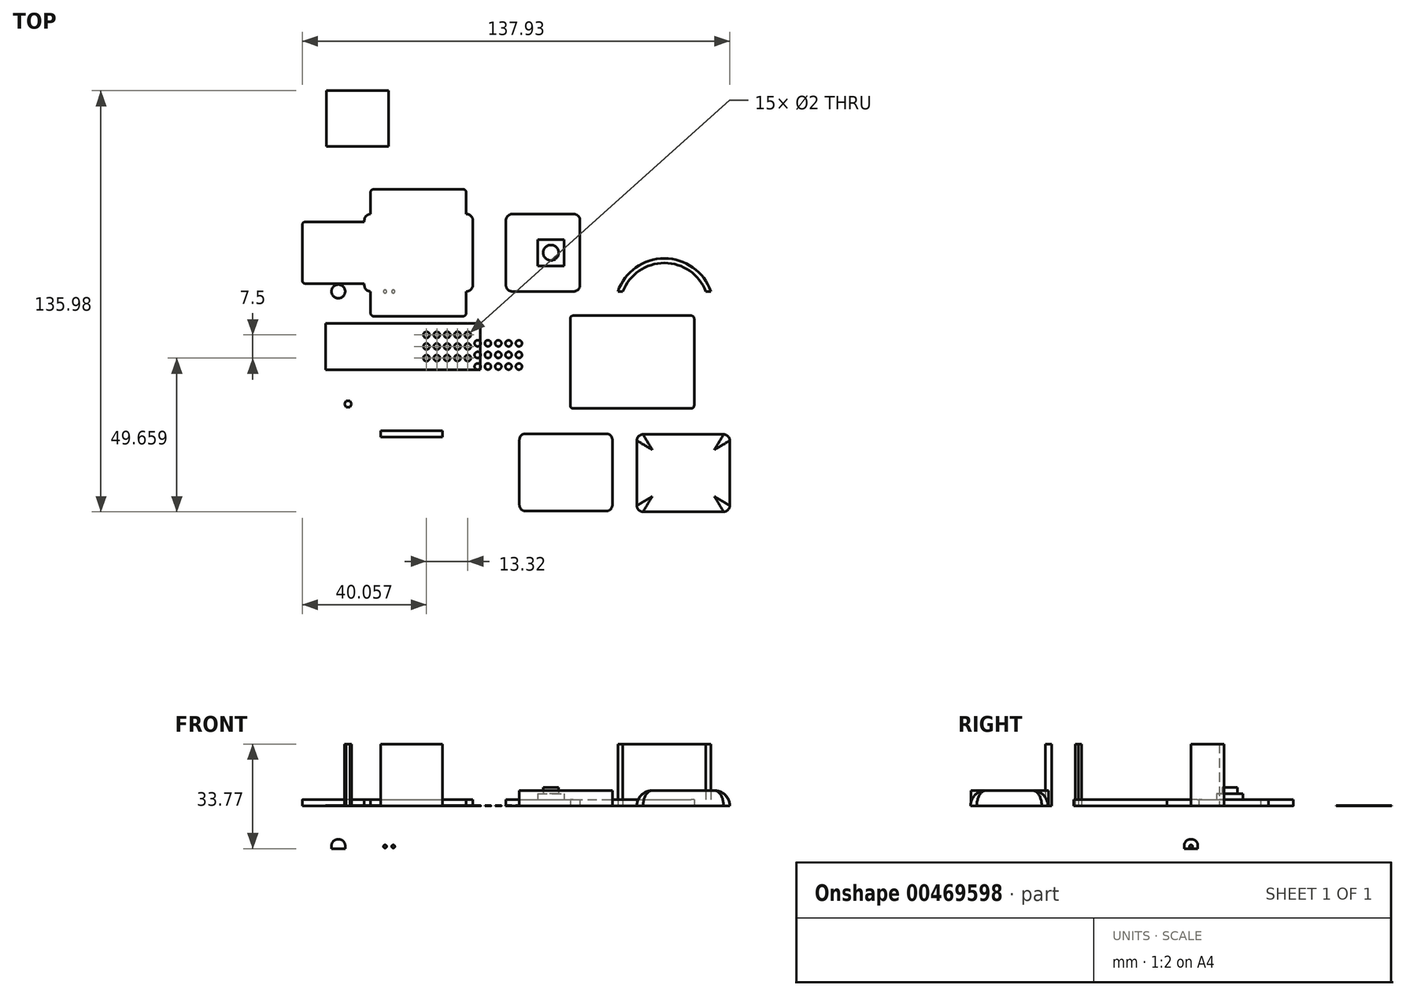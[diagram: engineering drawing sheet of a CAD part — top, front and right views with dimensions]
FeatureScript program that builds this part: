
annotation { "Feature Type Name" : "Feature", "Feature Type Description" : "" }
export const myFeature = defineFeature(function(context is Context, id is Id, definition is map)
    precondition{}
    {
        {
            var Q0;
            Q0=qCreatedBy(makeId("Top.planeOp"),FACE);
            var sketch = newSketch(context, id + "F0", { "sketchPlane" : qUnion([Q0])});
            skLineSegment(sketch, "E0.bottom", {"start": v(2, 0) * mm, "end": v(21.86, 0) * mm});
            skLineSegment(sketch, "E0.top", {"start": v(2, 25) * mm, "end": v(21.86, 25) * mm});
            skLineSegment(sketch, "E0.left", {"start": v(0, 2) * mm, "end": v(0, 23) * mm});
            skLineSegment(sketch, "E0.right", {"start": v(23.86, 2) * mm, "end": v(23.86, 23) * mm});
            skPoint(sketch, "E1.visualSharp", {"position": v(0, 25) * mm});
            skArc(sketch, "E1.filletArc", {"start": v(2, 25) * mm, "mid": v(0.59, 24.41) * mm, "end": v(0, 23) * mm});
            skPoint(sketch, "E2.visualSharp", {"position": v(0, 0) * mm});
            skArc(sketch, "E2.filletArc", {"start": v(0, 2) * mm, "mid": v(0.59, 0.59) * mm, "end": v(2, 0) * mm});
            skPoint(sketch, "E3.visualSharp", {"position": v(23.86, 25) * mm});
            skArc(sketch, "E3.filletArc", {"start": v(23.86, 23) * mm, "mid": v(23.28, 24.41) * mm, "end": v(21.86, 25) * mm});
            skPoint(sketch, "E4.visualSharp", {"position": v(23.86, 0) * mm});
            skArc(sketch, "E4.filletArc", {"start": v(21.86, 0) * mm, "mid": v(23.28, 0.59) * mm, "end": v(23.86, 2) * mm});
            skPoint(sketch, "E5.startSnap0", {"position": v(0.59, 0.59) * mm});
            skLineSegment(sketch, "E6", {"start": v(0, 25) * mm, "end": v(14.5, 25) * mm});
            skLineSegment(sketch, "E7", {"start": v(0, 0) * mm, "end": v(14.5, 0) * mm});
            skLineSegment(sketch, "E8", {"start": v(10.25, 12.5) * mm, "end": v(10.25, 16.75) * mm});
            skLineSegment(sketch, "E9.bottom", {"start": v(10.25, 16.75) * mm, "end": v(18.75, 16.75) * mm});
            skLineSegment(sketch, "E9.top", {"start": v(10.25, 8.25) * mm, "end": v(18.75, 8.25) * mm});
            skLineSegment(sketch, "E9.left", {"start": v(10.25, 16.75) * mm, "end": v(10.25, 8.25) * mm});
            skLineSegment(sketch, "E9.right", {"start": v(18.75, 16.75) * mm, "end": v(18.75, 8.25) * mm});
            skCircle(sketch, "E10", {"center": v(14.5, 12.5) * mm, "radius": 2.5 * mm});
            skPoint(sketch, "E10.centerSnap0", {"position": v(14.5, 16.75) * mm});
            skSolve(sketch);
        }
        {
            var Q0;
            Q0 = qSketchRegion(id + "F0", true);
            extrude(context, id + "F1", {"entities" : qUnion([Q0]), "depth" : 2 * mm});
        }
        {
            var Q0;
            {var subQ3=sQuery(id+"F0.wireOp",EDGE,"E9.bottom");Q0=makeQuery(id+"F0.imprint","IMPRINT",FACE,{"disambiguationData":[TD([[makeQuery(id+"F0.imprint","IMPRINT",EDGE,{"derivedFrom":subQ3}),-1.0]])]});}
            extrude(context, id + "F2", {"entities" : qUnion([Q0]), "operationType" : NewBodyOperationType.ADD, "depth" : 4 * mm});
        }
        {
            var Q0;
            Q0=makeQuery(id+"F0.imprint","IMPRINT",FACE,{"disambiguationData":[TD([[makeQuery(id+"F0.imprint","IMPRINT",EDGE,{"derivedFrom":sQuery(id+"F0.wireOp",EDGE,"E10")}),1.0]])]});
            extrude(context, id + "F3", {"entities" : qUnion([Q0]), "operationType" : NewBodyOperationType.ADD, "depth" : 6 * mm});
        }
        {
            var Q0;
            Q0=qCreatedBy(makeId("Top.planeOp"),FACE);
            var sketch = newSketch(context, id + "F4", { "sketchPlane" : qUnion([Q0])});
            skLineSegment(sketch, "E11.bottom", {"start": v(-43.71, 0) * mm, "end": v(-12.71, 0) * mm});
            skLineSegment(sketch, "E11.top", {"start": v(-43.71, 25) * mm, "end": v(-12.71, 25) * mm});
            skLineSegment(sketch, "E11.left", {"start": v(-45.71, 0) * mm, "end": v(-45.71, 23) * mm});
            skLineSegment(sketch, "E11.right", {"start": v(-10.71, 2) * mm, "end": v(-10.71, 23) * mm});
            skLineSegment(sketch, "E12", {"start": v(-45.71, 2) * mm, "end": v(-45.71, 2.5) * mm});
            skLineSegment(sketch, "E13.bottom", {"start": v(-45.71, 2.5) * mm, "end": v(-64.71, 2.5) * mm});
            skLineSegment(sketch, "E13.top", {"start": v(-45.71, 22.5) * mm, "end": v(-64.71, 22.5) * mm});
            skLineSegment(sketch, "E13.left", {"start": v(-45.71, 2.5) * mm, "end": v(-45.71, 22.5) * mm});
            skLineSegment(sketch, "E13.right", {"start": v(-65.71, 3.5) * mm, "end": v(-65.71, 21.5) * mm});
            skPoint(sketch, "E14.visualSharp", {"position": v(-45.71, 25) * mm});
            skArc(sketch, "E14.filletArc", {"start": v(-43.71, 25) * mm, "mid": v(-45.13, 24.41) * mm, "end": v(-45.71, 23) * mm});
            skPoint(sketch, "E15.visualSharp", {"position": v(-45.71, 0) * mm});
            skArc(sketch, "E15.filletArc", {"start": v(-45.71, 2) * mm, "mid": v(-45.13, 0.59) * mm, "end": v(-43.71, 0) * mm});
            skPoint(sketch, "E16.visualSharp", {"position": v(-10.71, 25) * mm});
            skArc(sketch, "E16.filletArc", {"start": v(-10.71, 23) * mm, "mid": v(-11.3, 24.41) * mm, "end": v(-12.71, 25) * mm});
            skPoint(sketch, "E17.visualSharp", {"position": v(-10.71, 0) * mm});
            skArc(sketch, "E17.filletArc", {"start": v(-12.71, 0) * mm, "mid": v(-11.3, 0.59) * mm, "end": v(-10.71, 2) * mm});
            skLineSegment(sketch, "E18.bottom", {"start": v(-43.71, 25) * mm, "end": v(-12.85, 25) * mm});
            skLineSegment(sketch, "E18.top", {"start": v(-42.71, 33) * mm, "end": v(-13.85, 33) * mm});
            skLineSegment(sketch, "E18.left", {"start": v(-43.71, 25) * mm, "end": v(-43.71, 32) * mm});
            skLineSegment(sketch, "E18.right", {"start": v(-12.85, 25) * mm, "end": v(-12.85, 32) * mm});
            skLineSegment(sketch, "E19.bottom", {"start": v(-43.71, 0) * mm, "end": v(-12.85, 0) * mm});
            skLineSegment(sketch, "E19.top", {"start": v(-42.71, -8) * mm, "end": v(-13.85, -8) * mm});
            skLineSegment(sketch, "E19.left", {"start": v(-43.71, 0) * mm, "end": v(-43.71, -7) * mm});
            skLineSegment(sketch, "E19.right", {"start": v(-12.85, 0) * mm, "end": v(-12.85, -7) * mm});
            skPoint(sketch, "E20.visualSharp", {"position": v(-65.71, 22.5) * mm});
            skArc(sketch, "E20.filletArc", {"start": v(-64.71, 22.5) * mm, "mid": v(-65.42, 22.2) * mm, "end": v(-65.71, 21.5) * mm});
            skPoint(sketch, "E21.visualSharp", {"position": v(-65.71, 2.5) * mm});
            skArc(sketch, "E21.filletArc", {"start": v(-65.71, 3.5) * mm, "mid": v(-65.42, 2.8) * mm, "end": v(-64.71, 2.5) * mm});
            skPoint(sketch, "E22.visualSharp", {"position": v(-43.71, -8) * mm});
            skArc(sketch, "E22.filletArc", {"start": v(-43.71, -7) * mm, "mid": v(-43.42, -7.7) * mm, "end": v(-42.71, -8) * mm});
            skPoint(sketch, "E23.visualSharp", {"position": v(-12.85, -8) * mm});
            skArc(sketch, "E23.filletArc", {"start": v(-13.85, -8) * mm, "mid": v(-13.14, -7.7) * mm, "end": v(-12.85, -7) * mm});
            skPoint(sketch, "E24.visualSharp", {"position": v(-43.71, 33) * mm});
            skArc(sketch, "E24.filletArc", {"start": v(-42.71, 33) * mm, "mid": v(-43.42, 32.7) * mm, "end": v(-43.71, 32) * mm});
            skPoint(sketch, "E25.visualSharp", {"position": v(-12.85, 33) * mm});
            skArc(sketch, "E25.filletArc", {"start": v(-12.85, 32) * mm, "mid": v(-13.14, 32.7) * mm, "end": v(-13.85, 33) * mm});
            skSolve(sketch);
        }
        {
            var Q0;
            Q0 = qSketchRegion(id + "F4", true);
            extrude(context, id + "F5", {"entities" : qUnion([Q0]), "depth" : 2 * mm});
        }
        {
            var Q0;
            Q0=qCreatedBy(makeId("Top.planeOp"),FACE);
            var sketch = newSketch(context, id + "F6", { "sketchPlane" : qUnion([Q0])});
            skLineSegment(sketch, "E26", {"start": v(36.12, 0) * mm, "end": v(37.72, 0) * mm});
            skArc(sketch, "E27", {"start": v(66.12, 0) * mm, "mid": v(51.12, 10.68) * mm, "end": v(36.12, 0) * mm});
            skArc(sketch, "E28.0", {"start": v(64.52, 0) * mm, "mid": v(51.12, 9.18) * mm, "end": v(37.72, 0) * mm});
            skLineSegment(sketch, "E29", {"start": v(37.72, 0) * mm, "end": v(36.12, 0) * mm});
            skLineSegment(sketch, "E30", {"start": v(64.52, 0) * mm, "end": v(66.12, 0) * mm});
            skSolve(sketch);
        }
        {
            var Q0;
            Q0 = qSketchRegion(id + "F6", true);
            extrude(context, id + "F7", {"entities" : qUnion([Q0]), "depth" : 20 * mm});
        }
        {
            var Q0;
            Q0=qCreatedBy(makeId("Top.planeOp"),FACE);
            var sketch = newSketch(context, id + "F8", { "sketchPlane" : qUnion([Q0])});
            skLineSegment(sketch, "E31.bottom", {"start": v(-8.26, -10.26) * mm, "end": v(-58.26, -10.26) * mm});
            skLineSegment(sketch, "E31.top", {"start": v(-8.26, -25.26) * mm, "end": v(-58.26, -25.26) * mm});
            skLineSegment(sketch, "E31.left", {"start": v(-8.26, -10.26) * mm, "end": v(-8.26, -25.26) * mm});
            skLineSegment(sketch, "E31.right", {"start": v(-58.26, -10.26) * mm, "end": v(-58.26, -25.26) * mm});
            skCircle(sketch, "E32", {"center": v(-25.65, -14.01) * mm, "radius": 1 * mm});
            skCircle(sketch, "E33", {"center": v(-22.32, -14.01) * mm, "radius": 1 * mm});
            skCircle(sketch, "E34", {"center": v(-18.98, -14.01) * mm, "radius": 1 * mm});
            skCircle(sketch, "E35", {"center": v(-15.66, -14.01) * mm, "radius": 1 * mm});
            skCircle(sketch, "E36", {"center": v(-12.33, -14.01) * mm, "radius": 1 * mm});
            skCircle(sketch, "E37", {"center": v(-15.66, -17.76) * mm, "radius": 1 * mm});
            skCircle(sketch, "E38", {"center": v(-12.33, -17.76) * mm, "radius": 1 * mm});
            skCircle(sketch, "E39", {"center": v(-18.98, -17.76) * mm, "radius": 1 * mm});
            skCircle(sketch, "E40", {"center": v(-25.65, -17.76) * mm, "radius": 1 * mm});
            skCircle(sketch, "E41", {"center": v(-22.32, -17.76) * mm, "radius": 1 * mm});
            skCircle(sketch, "E42", {"center": v(-25.65, -21.51) * mm, "radius": 1 * mm});
            skCircle(sketch, "E43", {"center": v(-22.32, -21.51) * mm, "radius": 1 * mm});
            skCircle(sketch, "E44", {"center": v(-18.98, -21.51) * mm, "radius": 1 * mm});
            skCircle(sketch, "E45", {"center": v(-15.66, -21.51) * mm, "radius": 1 * mm});
            skCircle(sketch, "E46", {"center": v(-12.33, -21.51) * mm, "radius": 1 * mm});
            skPoint(sketch, "E47.orphan", {"position": v(-34.93, -10.26) * mm});
            skPoint(sketch, "E48.orphan", {"position": v(-31.6, -10.26) * mm});
            skPoint(sketch, "E49.orphan", {"position": v(-28.27, -10.26) * mm});
            skSolve(sketch);
        }
        {
            var Q0;
            Q0 = qSketchRegion(id + "F8", true);
            extrude(context, id + "F9", {"entities" : qUnion([Q0]), "depth" : 0.1 * mm});
        }
        {
            var Q0;
            Q0=qCreatedBy(makeId("Top.planeOp"),FACE);
            var sketch = newSketch(context, id + "F10", { "sketchPlane" : qUnion([Q0])});
            skCircle(sketch, "E50", {"center": v(-9.16, -16.75) * mm, "radius": 1 * mm});
            skCircle(sketch, "E51", {"center": v(-5.83, -16.75) * mm, "radius": 1 * mm});
            skCircle(sketch, "E52", {"center": v(-2.49, -16.75) * mm, "radius": 1 * mm});
            skCircle(sketch, "E53", {"center": v(0.83, -16.75) * mm, "radius": 1 * mm});
            skCircle(sketch, "E54", {"center": v(4.16, -16.75) * mm, "radius": 1 * mm});
            skCircle(sketch, "E55", {"center": v(0.83, -20.5) * mm, "radius": 1 * mm});
            skCircle(sketch, "E56", {"center": v(4.16, -20.5) * mm, "radius": 1 * mm});
            skCircle(sketch, "E57", {"center": v(-2.49, -20.5) * mm, "radius": 1 * mm});
            skCircle(sketch, "E58", {"center": v(-9.16, -20.5) * mm, "radius": 1 * mm});
            skCircle(sketch, "E59", {"center": v(-5.83, -20.5) * mm, "radius": 1 * mm});
            skCircle(sketch, "E60", {"center": v(-9.16, -24.25) * mm, "radius": 1 * mm});
            skCircle(sketch, "E61", {"center": v(-5.83, -24.25) * mm, "radius": 1 * mm});
            skCircle(sketch, "E62", {"center": v(-2.49, -24.25) * mm, "radius": 1 * mm});
            skCircle(sketch, "E63", {"center": v(0.83, -24.25) * mm, "radius": 1 * mm});
            skCircle(sketch, "E64", {"center": v(4.16, -24.25) * mm, "radius": 1 * mm});
            skSolve(sketch);
        }
        {
            var Q0;
            Q0 = qSketchRegion(id + "F10", true);
            extrude(context, id + "F11", {"entities" : qUnion([Q0]), "depth" : 0.1 * mm});
        }
        {
            var Q0;
            Q0=qCreatedBy(makeId("Top.planeOp"),FACE);
            var sketch = newSketch(context, id + "F12", { "sketchPlane" : qUnion([Q0])});
            skLineSegment(sketch, "E65.bottom", {"start": v(21.72, -7.8) * mm, "end": v(59.72, -7.8) * mm});
            skLineSegment(sketch, "E65.top", {"start": v(21.72, -37.8) * mm, "end": v(59.72, -37.8) * mm});
            skLineSegment(sketch, "E65.left", {"start": v(20.72, -8.8) * mm, "end": v(20.72, -36.8) * mm});
            skLineSegment(sketch, "E65.right", {"start": v(60.72, -8.8) * mm, "end": v(60.72, -36.8) * mm});
            skPoint(sketch, "E66.visualSharp", {"position": v(20.72, -7.8) * mm});
            skArc(sketch, "E66.filletArc", {"start": v(21.72, -7.8) * mm, "mid": v(21.01, -8.1) * mm, "end": v(20.72, -8.8) * mm});
            skPoint(sketch, "E67.visualSharp", {"position": v(60.72, -7.8) * mm});
            skArc(sketch, "E67.filletArc", {"start": v(60.72, -8.8) * mm, "mid": v(60.43, -8.1) * mm, "end": v(59.72, -7.8) * mm});
            skPoint(sketch, "E68.visualSharp", {"position": v(60.72, -37.8) * mm});
            skArc(sketch, "E68.filletArc", {"start": v(59.72, -37.8) * mm, "mid": v(60.43, -37.51) * mm, "end": v(60.72, -36.8) * mm});
            skPoint(sketch, "E69.visualSharp", {"position": v(20.72, -37.8) * mm});
            skArc(sketch, "E69.filletArc", {"start": v(20.72, -36.8) * mm, "mid": v(21.01, -37.51) * mm, "end": v(21.72, -37.8) * mm});
            skSolve(sketch);
        }
        {
            var Q0;
            Q0=makeQuery(id+"F12.imprint","IMPRINT",FACE,{"disambiguationData":[TD([[makeQuery(id+"F12.imprint","IMPRINT",EDGE,{"derivedFrom":sQuery(id+"F12.wireOp",EDGE,"E65.bottom")}),-1.0]])]});
            extrude(context, id + "F13", {"entities" : qUnion([Q0]), "depth" : 2 * mm});
        }
        {
            var Q0;
            Q0=qCreatedBy(makeId("Top.planeOp"),FACE);
            var sketch = newSketch(context, id + "F14", { "sketchPlane" : qUnion([Q0])});
            skCircle(sketch, "E70.cCircle", {"center": v(-50.98, -36.34) * mm, "radius": 1 * mm, "construction": true});
            skLineSegment(sketch, "E70.0", {"start": v(-50.4, -37.34) * mm, "end": v(-51.55, -37.34) * mm});
            skLineSegment(sketch, "E70.1", {"start": v(-51.55, -37.34) * mm, "end": v(-52.13, -36.34) * mm});
            skLineSegment(sketch, "E70.2", {"start": v(-52.13, -36.34) * mm, "end": v(-51.55, -35.34) * mm});
            skLineSegment(sketch, "E70.3", {"start": v(-51.55, -35.34) * mm, "end": v(-50.4, -35.34) * mm});
            skLineSegment(sketch, "E70.4", {"start": v(-50.4, -35.34) * mm, "end": v(-49.82, -36.34) * mm});
            skLineSegment(sketch, "E70.5", {"start": v(-49.82, -36.34) * mm, "end": v(-50.4, -37.34) * mm});
            skPoint(sketch, "E70.0.midPoint", {"position": v(-50.98, -37.34) * mm});
            skSolve(sketch);
        }
        {
            var Q0;
            Q0 = qSketchRegion(id + "F14", true);
            extrude(context, id + "F15", {"entities" : qUnion([Q0]), "depth" : 20 * mm});
        }
        {
            var Q0;
            Q0=qCreatedBy(makeId("Top.planeOp"),FACE);
            var sketch = newSketch(context, id + "F16", { "sketchPlane" : qUnion([Q0])});
            skLineSegment(sketch, "E71.bottom", {"start": v(-40.48, -45.03) * mm, "end": v(-20.48, -45.03) * mm});
            skLineSegment(sketch, "E71.top", {"start": v(-40.48, -47.03) * mm, "end": v(-20.48, -47.03) * mm});
            skLineSegment(sketch, "E71.left", {"start": v(-40.48, -45.03) * mm, "end": v(-40.48, -47.03) * mm});
            skLineSegment(sketch, "E71.right", {"start": v(-20.48, -45.03) * mm, "end": v(-20.48, -47.03) * mm});
            skSolve(sketch);
        }
        {
            var Q0;
            Q0=qCreatedBy(makeId("Top.planeOp"),FACE);
            var sketch = newSketch(context, id + "F17", { "sketchPlane" : qUnion([Q0])});
            skLineSegment(sketch, "E72.bottom", {"start": v(6.32, -45.95) * mm, "end": v(32.32, -45.95) * mm});
            skLineSegment(sketch, "E72.top", {"start": v(6.32, -70.95) * mm, "end": v(32.32, -70.95) * mm});
            skLineSegment(sketch, "E72.left", {"start": v(4.32, -47.95) * mm, "end": v(4.32, -68.95) * mm});
            skLineSegment(sketch, "E72.right", {"start": v(34.32, -47.95) * mm, "end": v(34.32, -68.95) * mm});
            skPoint(sketch, "E73.visualSharp", {"position": v(4.32, -45.95) * mm});
            skArc(sketch, "E73.filletArc", {"start": v(6.32, -45.95) * mm, "mid": v(4.91, -46.53) * mm, "end": v(4.32, -47.95) * mm});
            skPoint(sketch, "E74.visualSharp", {"position": v(4.32, -70.95) * mm});
            skArc(sketch, "E74.filletArc", {"start": v(4.32, -68.95) * mm, "mid": v(4.91, -70.36) * mm, "end": v(6.32, -70.95) * mm});
            skPoint(sketch, "E75.visualSharp", {"position": v(34.32, -45.95) * mm});
            skArc(sketch, "E75.filletArc", {"start": v(34.32, -47.95) * mm, "mid": v(33.74, -46.53) * mm, "end": v(32.32, -45.95) * mm});
            skPoint(sketch, "E76.visualSharp", {"position": v(34.32, -70.95) * mm});
            skArc(sketch, "E76.filletArc", {"start": v(32.32, -70.95) * mm, "mid": v(33.74, -70.36) * mm, "end": v(34.32, -68.95) * mm});
            skSolve(sketch);
        }
        {
            var Q0;
            Q0=makeQuery(id+"F17.imprint","IMPRINT",FACE,{"disambiguationData":[TD([[makeQuery(id+"F17.imprint","IMPRINT",EDGE,{"derivedFrom":sQuery(id+"F17.wireOp",EDGE,"E72.bottom")}),-1.0]])]});
            extrude(context, id + "F18", {"entities" : qUnion([Q0]), "depth" : 5 * mm});
        }
        {
            var Q0;
            Q0=qCreatedBy(makeId("Top.planeOp"),FACE);
            var sketch = newSketch(context, id + "F19", { "sketchPlane" : qUnion([Q0])});
            skLineSegment(sketch, "E77.bottom", {"start": v(44.22, -46.17) * mm, "end": v(70.22, -46.17) * mm});
            skLineSegment(sketch, "E77.top", {"start": v(44.22, -71.17) * mm, "end": v(70.22, -71.17) * mm});
            skLineSegment(sketch, "E77.left", {"start": v(42.22, -48.17) * mm, "end": v(42.22, -69.17) * mm});
            skLineSegment(sketch, "E77.right", {"start": v(72.22, -48.17) * mm, "end": v(72.22, -69.17) * mm});
            skPoint(sketch, "E78.visualSharp", {"position": v(42.22, -46.17) * mm});
            skArc(sketch, "E78.filletArc", {"start": v(44.22, -46.17) * mm, "mid": v(42.81, -46.75) * mm, "end": v(42.22, -48.17) * mm});
            skPoint(sketch, "E79.visualSharp", {"position": v(42.22, -71.17) * mm});
            skArc(sketch, "E79.filletArc", {"start": v(42.22, -69.17) * mm, "mid": v(42.81, -70.58) * mm, "end": v(44.22, -71.17) * mm});
            skPoint(sketch, "E80.visualSharp", {"position": v(72.22, -46.17) * mm});
            skArc(sketch, "E80.filletArc", {"start": v(72.22, -48.17) * mm, "mid": v(71.64, -46.75) * mm, "end": v(70.22, -46.17) * mm});
            skPoint(sketch, "E81.visualSharp", {"position": v(72.22, -71.17) * mm});
            skArc(sketch, "E81.filletArc", {"start": v(70.22, -71.17) * mm, "mid": v(71.64, -70.58) * mm, "end": v(72.22, -69.17) * mm});
            skSolve(sketch);
        }
        {
            var Q0;
            Q0 = qSketchRegion(id + "F19", true);
            extrude(context, id + "F20", {"entities" : qUnion([Q0]), "depth" : 5 * mm});
        }
        {
            var Q0;
            Q0=makeQuery(id+"F20.opExtrude","CAP_EDGE",EDGE,{"disambiguationData":[OSD([sQuery(id+"F19.wireOp",EDGE,"E77.left")])],"isStart":false});
            fillet(context, id + "F21", {"entities" : qUnion([Q0]), "radius" : 5 * mm, "tangentPropagation" : true, "allowEdgeOverflow" : false});
        }
        {
            var Q0;
            Q0=makeQuery(id+"F16.imprint","IMPRINT",FACE,{"disambiguationData":[TD([[makeQuery(id+"F16.imprint","IMPRINT",EDGE,{"derivedFrom":sQuery(id+"F16.wireOp",EDGE,"E71.bottom")}),-1.0]])]});
            extrude(context, id + "F22", {"entities" : qUnion([Q0]), "depth" : 20 * mm});
        }
        {
            var Q0;
            Q0=qCreatedBy(makeId("Front.planeOp"),FACE);
            var sketch = newSketch(context, id + "F23", { "sketchPlane" : qUnion([Q0])});
            skLineSegment(sketch, "E82.bottom", {"start": v(-54.3, -10.77) * mm, "end": v(-54.1, -10.77) * mm});
            skLineSegment(sketch, "E82.top", {"start": v(-56.3, -13.77) * mm, "end": v(-54.1, -13.77) * mm});
            skLineSegment(sketch, "E82.left", {"start": v(-56.3, -12.77) * mm, "end": v(-56.3, -13.77) * mm});
            skLineSegment(sketch, "E82.right", {"start": v(-54.1, -10.77) * mm, "end": v(-54.1, -13.77) * mm});
            skPoint(sketch, "E83.visualSharp", {"position": v(-56.3, -10.77) * mm});
            skArc(sketch, "E83.filletArc", {"start": v(-54.3, -10.77) * mm, "mid": v(-55.72, -11.36) * mm, "end": v(-56.3, -12.77) * mm});
            skSolve(sketch);
        }
        {
            var Q0;
            Q0=makeQuery(id+"F23.imprint","IMPRINT",FACE,{"disambiguationData":[TD([[makeQuery(id+"F23.imprint","IMPRINT",EDGE,{"derivedFrom":sQuery(id+"F23.wireOp",EDGE,"E82.bottom")}),-1.0]])]});
            var Q1;
            Q1=sQuery(id+"F23.wireOp",EDGE,"E82.right");
            revolve(context, id + "F24", {"entities" : qUnion([Q0]), "axis" : qUnion([Q1]), "revolveType" : RevolveType.FULL});
        }
        {
            var Q0;
            Q0=qCreatedBy(makeId("Front.planeOp"),FACE);
            var sketch = newSketch(context, id + "F25", { "sketchPlane" : qUnion([Q0])});
            skArc(sketch, "E84", {"start": v(-39.02, -12.59) * mm, "mid": v(-39.52, -13.09) * mm, "end": v(-39.02, -13.59) * mm});
            skLineSegment(sketch, "E85", {"start": v(-39.02, -13.09) * mm, "end": v(-39.02, -12.59) * mm});
            skLineSegment(sketch, "E86", {"start": v(-39.02, -13.09) * mm, "end": v(-39.02, -13.59) * mm});
            skSolve(sketch);
        }
        {
            var Q0;
            Q0 = qSketchRegion(id + "F25", true);
            var Q1;
            Q1=sQuery(id+"F25.wireOp",EDGE,"E86");
            revolve(context, id + "F26", {"entities" : qUnion([Q0]), "axis" : qUnion([Q1]), "revolveType" : RevolveType.FULL});
        }
        {
            var Q0;
            Q0=qCreatedBy(makeId("Front.planeOp"),FACE);
            var sketch = newSketch(context, id + "F27", { "sketchPlane" : qUnion([Q0])});
            skArc(sketch, "E87", {"start": v(-36.39, -12.6) * mm, "mid": v(-36.89, -13.1) * mm, "end": v(-36.39, -13.6) * mm});
            skLineSegment(sketch, "E88", {"start": v(-36.39, -13.1) * mm, "end": v(-36.39, -12.6) * mm});
            skLineSegment(sketch, "E89", {"start": v(-36.39, -13.1) * mm, "end": v(-36.39, -13.6) * mm});
            skSolve(sketch);
        }
        {
            var Q0;
            Q0 = qSketchRegion(id + "F27", true);
            var Q1;
            Q1=sQuery(id+"F27.wireOp",EDGE,"E88");
            revolve(context, id + "F28", {"entities" : qUnion([Q0]), "axis" : qUnion([Q1]), "revolveType" : RevolveType.FULL});
        }
        {
            var Q0;
            Q0=qCreatedBy(makeId("Top.planeOp"),FACE);
            var sketch = newSketch(context, id + "F29", { "sketchPlane" : qUnion([Q0])});
            skLineSegment(sketch, "E90.bottom", {"start": v(-57.93, 64.8) * mm, "end": v(-37.93, 64.8) * mm});
            skLineSegment(sketch, "E90.top", {"start": v(-57.93, 46.8) * mm, "end": v(-37.93, 46.8) * mm});
            skLineSegment(sketch, "E90.left", {"start": v(-57.93, 64.8) * mm, "end": v(-57.93, 46.8) * mm});
            skLineSegment(sketch, "E90.right", {"start": v(-37.93, 64.8) * mm, "end": v(-37.93, 46.8) * mm});
            skSolve(sketch);
        }
        {
            var Q0;
            Q0 = qSketchRegion(id + "F29", true);
            extrude(context, id + "F30", {"entities" : qUnion([Q0]), "depth" : 0.1 * mm});
        }
    });
